# Revit family: Little Amp_Bfit 1250C_V-1500C_V Boiler and Water Heater
name_source: partatom
category: Mechanical Equipment
units: mm (PartAtom-declared; Revit-internal decimal feet)

## family parameters
Always vertical = Yes
Classification Number = 23.75.00.00
Cut with Voids When Loaded = No
Maintain Annotation Orientation = No
Part Type = Normal
Room Calculation Point = No
Round Connector Dimension = Use Diameter
Shared = No
Work Plane-Based = No

## types (2) — shared parameters
Air Supply = 6"
Air Supply I.D. = 5 19/32"
Air Supply Length = 1 7/16"
Air Supply O.D. = 5 7/8"
Air Supply X = 5 5/8"
Air Supply Y = 14"
Boiler Drain = 3/4" NPT Female
Condensate Trap = 1" Pipe
Default Elevation = 0"
Gas Train = 1 1/4" NPT Female
Gas Train Ball Valve Dia. = 2 11/32"
Gas Train Ball Valve X = 23"
Gas Train Ball Valve Y = 29 3/4"
Gas Train Dia. = 1 21/32"
Gas Train X = 23"
Gas Train Y = 29 3/4"
Height = 40 1/4"
Hydronic Return = 2" NPT Male
Hydronic Supply = 2" NPT Female
Length = 55 1/8"
Manufacturer = Bryan Steam
Vent = 8"
Vent I.D. = 8"
Vent Length = 7 3/8"
Vent O.D. = 8 5/32"
Vent X = 16 1/8"
Vent Y = 21 5/8"
Width = 26 1/8"

## type names (no varying parameters)
- AMP 1250C/V Boiler and Water Heater
- AMP 1500C/V Boiler and Water Heater

## geometry (parser evidence)
native form markers: Sweep x2
no freeform markers — native parametric forms only
